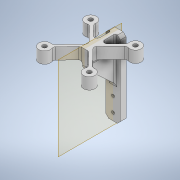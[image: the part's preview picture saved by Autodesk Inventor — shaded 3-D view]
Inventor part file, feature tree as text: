
AUTODESK INVENTOR PART (.ipt)
format: ipt  version: 2020 (Build 240168000, 168)  size: 485,376 bytes
history: native  units: mm
features: projected_geometry x15, extrude x10, sketch x10, fillet x6, thicken_offset x5, other x3, chamfer x2, plane x1, reference x1
ambient origin geometry x8: Origin, YZ Plane, XZ Plane, XY Plane, X Axis, Y Axis, Z Axis, Center Point
bodies: Solid1 (feature_tree)
feature tree (53):
  extrude  "Extrusion1"  Depth=10.0mm
  extrude  "Extrusion2"  Depth=2.0mm
  plane  "Work Plane1"
  extrude  "Extrusion3"  Depth=10.0mm
  extrude  "Extrusion4"  Depth=20.0mm
  extrude  "Extrusion5"  Depth=40.0mm
  extrude  "Extrusion6"  Depth=30.0mm
  extrude  "Extrusion7"  Depth=3.0mm TaperAngle=0.0deg
  extrude  "Extrusion8"  Depth=32.0mm
  chamfer  "Chamfer1"  Distance=3.0mm
  extrude  "Extrusion9"  Depth=2.0mm
  fillet  "Fillet3"  Radius=3.0mm
  fillet  "Fillet4"  Radius=8.0mm
  fillet  "Fillet5"  Radius=8.0mm
  thicken_offset  "Thicken1"
  extrude  "Extrusion14"  Depth=2.0mm
  thicken_offset  "Thicken2"
  thicken_offset  "Thicken3"
  thicken_offset  "Thicken4"
  thicken_offset  "Thicken5"
  fillet  "Fillet14"  Radius=8.0mm
  fillet  "Fillet15"  Radius=5.0mm
  fillet  "Fillet16"  Radius=3.0mm
  chamfer  "Chamfer2"  Distance=3.0mm
  sketch  "Sketch1"  dims[d0=10.0mm d1=20.0mm]
  reference  "Reference1"
  sketch  "Sketch2"  dims[d2=2.0mm d3=2.0mm]
  projected_geometry  "Projected Loop1"
  sketch  "Sketch3"  dims[d4=10.0mm d5=30.0mm]
  projected_geometry  "Projected Loop2"
  projected_geometry  "Projected Loop3"
  sketch  "Sketch4"  dims[d6=3.0mm d7=0.0mm d8=20.0mm]
  projected_geometry  "Projected Loop4"
  sketch  "Sketch5"  dims[d9=40.0mm d10=40.0mm]
  projected_geometry  "Projected Loop5"
  sketch  "Sketch6"  dims[d11=3.0mm d12=0.0mm d13=30.0mm]
  projected_geometry  "Projected Loop6"
  sketch  "Sketch7"  dims[d14=28.0mm d15=3.0mm d16=0.0mm]
  projected_geometry  "Projected Loop7"
  projected_geometry  "Projected Loop8"
  projected_geometry  "Projected Loop9"
  projected_geometry  "Projected Loop10"
  projected_geometry  "Projected Loop11"
  sketch  "Sketch8"  dims[d17=31.0mm d18=32.0mm]
  projected_geometry  "Projected Loop12"
  sketch  "Sketch9"  dims[d19=3.0mm]
  projected_geometry  "Projected Loop13"
  sketch  "Sketch14"  dims[d20=3.0mm d21=3.0mm d22=3.0mm d23=3.0mm d24=0.0mm d25=8.0mm d26=8.0mm d27=8.0mm d28=8.0mm d29=5.0mm d30=0.0mm d31=3.0mm d32=3.0mm d33=5.0mm d34=0.0mm d35=5.0mm d36=0.0mm d37=20.0mm d38=0.0mm d39=2.0mm d40=2.0mm d41=45.0deg d42=20.0mm d43=0.0mm d46=3.0mm d47=1.0mm d48=3.0mm d55=1.0mm d56=1.0mm d78=8.0mm d79=8.0mm d80=10.0mm d81=0.0mm d82=1.0mm d83=1.0mm d84=1.0mm d85=1.0mm d86=1.0mm d87=1.0mm d88=1.0mm d89=1.0mm d90=2.0mm d91=2.0mm d92=2.0mm d93=2.0mm d94=2.0mm d95=45.0deg]
  projected_geometry  "Projected Loop21"
  projected_geometry  "Projected Loop22"
  parser-record x1  (decoder bookkeeping rows leaked as tree rows — omitted from the tree; the rows remain in map.json)
  other  "leg_1.iam"
  other  "leg_holder_2:1"
note: 1 file-system path scrubbed to <path> (originals preserved in map.json)
